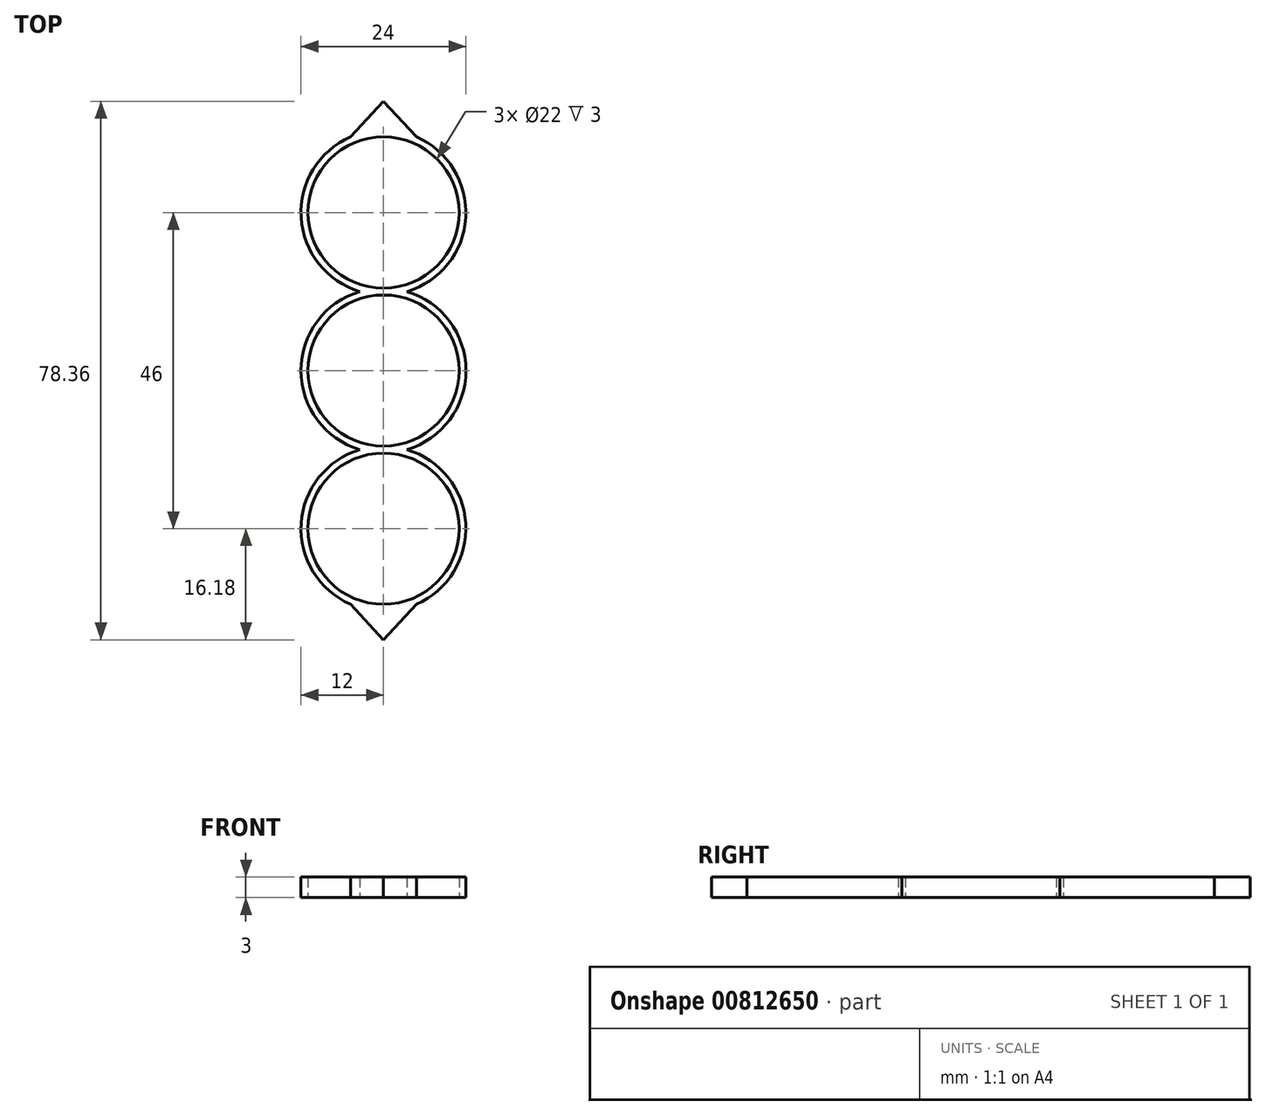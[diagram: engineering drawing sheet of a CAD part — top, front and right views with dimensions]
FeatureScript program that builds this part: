
annotation { "Feature Type Name" : "Feature", "Feature Type Description" : "" }
export const myFeature = defineFeature(function(context is Context, id is Id, definition is map)
    precondition{}
    {
        {
            var Q0;
            Q0=qCreatedBy(makeId("Top.planeOp"),FACE);
            var sketch = newSketch(context, id + "F0", { "sketchPlane" : qUnion([Q0])});
            skArc(sketch, "E0", {"start": v(-3.43, 11.5) * mm, "mid": v(-12, 0) * mm, "end": v(-3.43, -11.5) * mm});
            skCircle(sketch, "E1", {"center": v(0, 0) * mm, "radius": 11 * mm});
            skArc(sketch, "E2", {"start": v(3.43, 11.5) * mm, "mid": v(11.98, 22.27) * mm, "end": v(4.8, 34) * mm});
            skCircle(sketch, "E3", {"center": v(0, 23) * mm, "radius": 11 * mm});
            skCircle(sketch, "E4.MirrorC", {"center": v(0, -23) * mm, "radius": 11 * mm});
            skArc(sketch, "E5.MirrorC", {"start": v(3.43, -11.5) * mm, "mid": v(11.98, -22.27) * mm, "end": v(4.8, -34) * mm});
            skArc(sketch, "E6.trimOffspring", {"start": v(3.43, -11.5) * mm, "mid": v(12, 0) * mm, "end": v(3.43, 11.5) * mm});
            skLineSegment(sketch, "E7", {"start": v(0, 39.18) * mm, "end": v(-4.8, 34) * mm});
            skLineSegment(sketch, "E8.MirrorCS", {"start": v(0, 39.18) * mm, "end": v(4.8, 34) * mm});
            skArc(sketch, "E9.trimOffspring", {"start": v(-4.8, 34) * mm, "mid": v(-11.98, 22.27) * mm, "end": v(-3.43, 11.5) * mm});
            skLineSegment(sketch, "E10.MirrorCS", {"start": v(0, -39.18) * mm, "end": v(-4.8, -34) * mm});
            skLineSegment(sketch, "E11.MirrorCS", {"start": v(0, -39.18) * mm, "end": v(4.8, -34) * mm});
            skArc(sketch, "E12.trimOffspring", {"start": v(-4.8, -34) * mm, "mid": v(-11.98, -22.27) * mm, "end": v(-3.43, -11.5) * mm});
            skSolve(sketch);
        }
        {
            var Q0;
            Q0=makeQuery(id+"F0.imprint","IMPRINT",FACE,{"disambiguationData":[TD([[makeQuery(id+"F0.imprint","IMPRINT",EDGE,{"derivedFrom":sQuery(id+"F0.wireOp",EDGE,"E0")}),1.0]])]});
            extrude(context, id + "F1", {"entities" : qUnion([Q0]), "depth" : 3 * mm, "offsetDistance" : 25 * mm});
        }
    });
